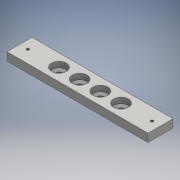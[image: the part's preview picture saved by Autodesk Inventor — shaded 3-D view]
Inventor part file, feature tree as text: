
AUTODESK INVENTOR PART (.ipt)
format: ipt  version: 2016 (Build 200138000, 138)  size: 123,392 bytes
history: native  units: mm
features: sketch x3, hole x2, extrude x1
ambient origin geometry x8: Origin, YZ Plane, XZ Plane, XY Plane, X Axis, Y Axis, Z Axis, Center Point
bodies: Solid1 (feature_tree)
feature tree (6):
  extrude  "Extrusion1"  Depth=170.0mm
  hole  "Hole1"  [1 undecoded]
  hole  "Hole2"  [1 undecoded]
  sketch  "Sketch1"  dims[d0=30.0mm d1=170.0mm]
  sketch  "Sketch2"  dims[d2=85.0mm d3=15.0mm]
  sketch  "Sketch3"  dims[d4=10.0mm d5=0.0mm d9=6.6mm d10=6.0mm d11=18.0mm d12=7.0mm d13=90.0deg d14=8.0mm d15=20.594885mm d16=150.0mm d17=75.0mm d19=3.242mm d20=8.0mm d21=19.05mm d22=4.775mm d23=90.0deg d24=11.8mm d25=20.594885mm d30=25.0mm d31=25.0mm d32=25.0mm d33=12.5mm]
note: 2 required parameter values undecoded (feature->parameter linkage not recoverable at this tier; creation-order binding heuristic only, values carry confidence <= 0.55)
